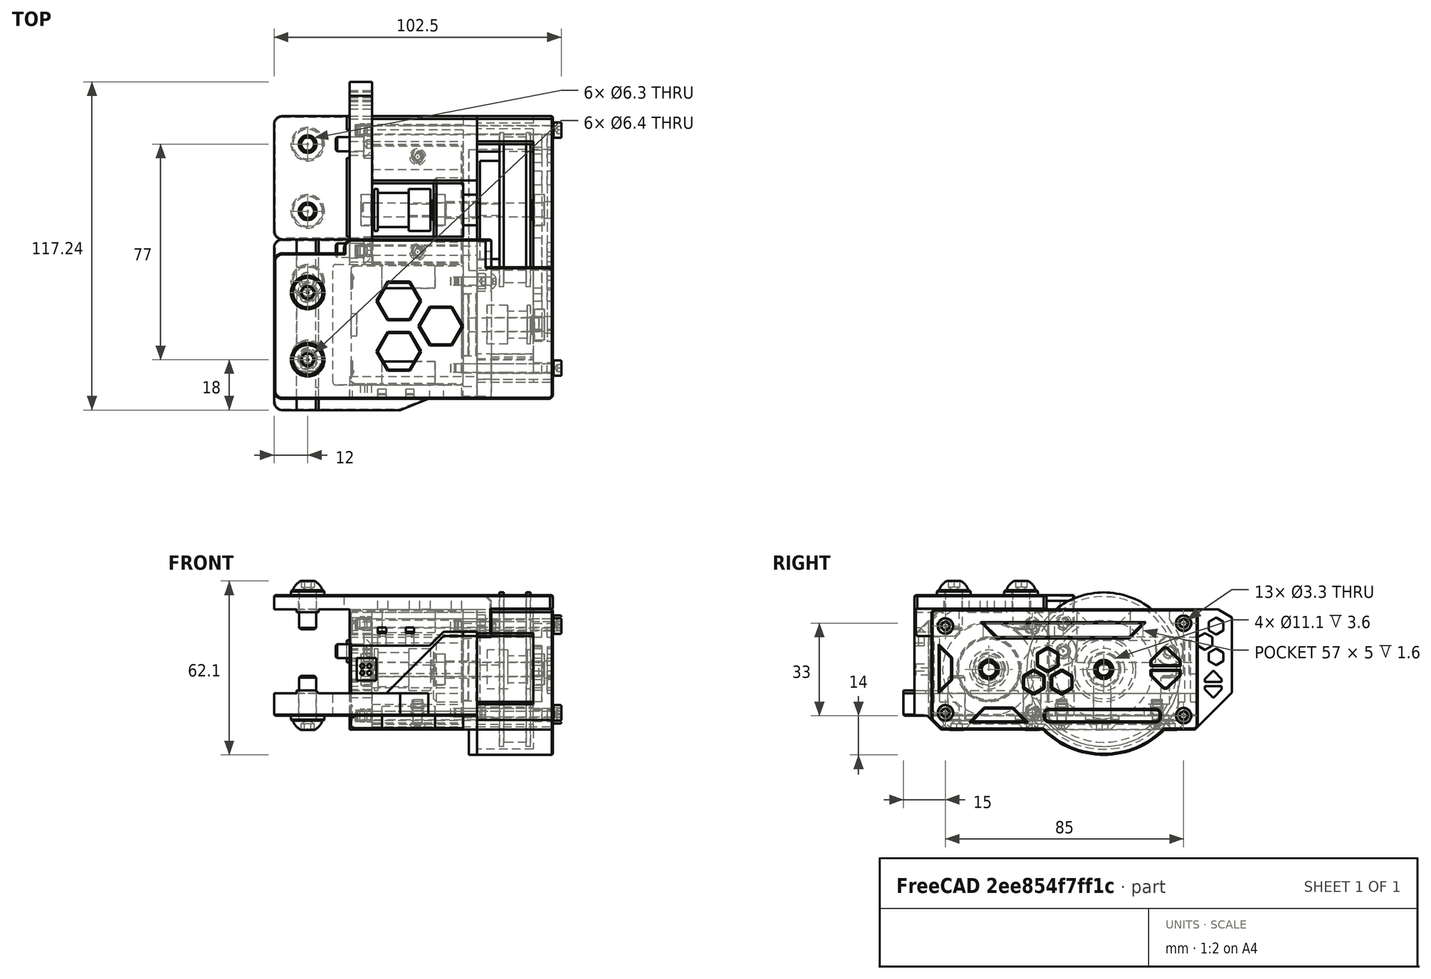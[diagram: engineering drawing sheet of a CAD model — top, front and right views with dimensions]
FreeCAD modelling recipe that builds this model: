
FCSTD DOCUMENT  (FreeCAD 0.19R24291 (Git))
Label: z-motor-right-assembly
License: Other
LicenseURL: GPL3
objects: Part::FeaturePython×27, Part::Feature×18, PartDesign::CoordinateSystem×1, App::Part×1
note: 46 computed .brp shape members not serialized (recipe doc carries the construction recipe); baked Part::Feature solids carry a one-line shape summary decoded from their .brp

FEATURE [Part::Feature] Cut001024010001  label="motor-spacer"
  shape: bbox 0.5 x 6.9 x 6.9 mm, 4 faces (baked)
FEATURE [Part::Feature] Cut001004001  label="MR115ZZ006"
  shape: bbox 4 x 11 x 11 mm, 4 faces (baked)
FEATURE [Part::Feature] Cut001024010002  label="20t-9mm-pulley001"
  shape: bbox 20 x 15 x 15 mm, 8 faces (baked)
FEATURE [Part::Feature] Cut001005001  label="MR115ZZ005"
  shape: bbox 4 x 11 x 11 mm, 4 faces (baked)
FEATURE [Part::Feature] Cut001024007001  label="motor-spacer001"
  shape: bbox 0.5 x 6.9 x 6.9 mm, 4 faces (baked)
FEATURE [Part::Feature] Cut001003001  label="MR115ZZ007"
  shape: bbox 4 x 11 x 11 mm, 4 faces (baked)
FEATURE [Part::Feature] Fusion006002011004053036004001001001  label="motor-40mm"
  shape: bbox 67 x 47 x 42 mm, 100 faces (baked)
FEATURE [Part::Feature] Cut001024009001  label="motor-spacer003"
  shape: bbox 0.5 x 6.9 x 6.9 mm, 4 faces (baked)
FEATURE [Part::Feature] Cut001024008001  label="motor-spacer004"
  shape: bbox 0.5 x 6.9 x 6.9 mm, 4 faces (baked)
FEATURE [Part::Feature] Cut001001001  label="16t-pulley001"
  shape: bbox 15.5 x 13.9 x 13.9 mm, 8 faces (baked)
FEATURE [Part::FeaturePython] Washer  label="M6-Washer"  # Fasteners workbench fastener (typed FeaturePython)
  Placement = pos=(-15,-12.5,35) rot=(0,0,1;0rad)
  diameter = 2
  invert = false
  matchOuter = true
  offset = 0
  type = 4
FEATURE [Part::FeaturePython] Washer001  label="M6-Washer011"  # Fasteners workbench fastener (typed FeaturePython)
  Placement = pos=(-15,11.5,35) rot=(0,0,1;0rad)
  diameter = 2
  invert = false
  matchOuter = true
  offset = 0
  type = 4
FEATURE [Part::FeaturePython] Washer002  label="M6-Washer009"  # Fasteners workbench fastener (typed FeaturePython)
  Placement = pos=(-15,-11.5,-8) rot=(1,0,0;3.14159rad)
  diameter = 2
  invert = true
  matchOuter = true
  offset = 0
  type = 4
FEATURE [Part::FeaturePython] Washer003  label="M6-Washer010"  # Fasteners workbench fastener (typed FeaturePython)
  Placement = pos=(-15,15.5,-8) rot=(1,0,0;3.14159rad)
  diameter = 2
  invert = true
  matchOuter = true
  offset = 0
  type = 4
FEATURE [Part::FeaturePython] Washer004  label="M6-Washer013"  # Fasteners workbench fastener (typed FeaturePython)
  Placement = pos=(-15,40.5,-8) rot=(1,0,0;3.14159rad)
  diameter = 2
  invert = true
  matchOuter = true
  offset = 0
  type = 4
FEATURE [Part::FeaturePython] Washer005  label="M6-Washer012"  # Fasteners workbench fastener (typed FeaturePython)
  Placement = pos=(-15,64.5,-8) rot=(1,0,0;3.14159rad)
  diameter = 2
  invert = true
  matchOuter = true
  offset = 0
  type = 4
FEATURE [Part::FeaturePython] Screw  label="M3x70-Screw"  # Fasteners workbench fastener (typed FeaturePython)
  Placement = pos=(72.5,69.5,-8) rot=(0,1,0;1.5708rad)
  diameter = 4
  invert = false
  length = 10
  lengthCustom = 70
  matchOuter = true
  offset = 0
  thread = false
  type = 33
FEATURE [Part::FeaturePython] Screw001  label="M3x35-Screw"  # Fasteners workbench fastener (typed FeaturePython)
  Placement = pos=(72.5,-15.5,-7) rot=(0,1,0;1.5708rad)
  diameter = 4
  invert = false
  length = 10
  lengthCustom = 35
  matchOuter = true
  offset = 0
  thread = false
  type = 33
FEATURE [Part::FeaturePython] Screw002  label="M3x35-Screw001"  # Fasteners workbench fastener (typed FeaturePython)
  Placement = pos=(72.5,-15.5,24) rot=(0,1,0;1.5708rad)
  diameter = 4
  invert = false
  length = 10
  lengthCustom = 35
  matchOuter = true
  offset = 0
  thread = false
  type = 33
FEATURE [Part::FeaturePython] Screw003  label="M3x70-Screw001"  # Fasteners workbench fastener (typed FeaturePython)
  Placement = pos=(72.5,69.5,25) rot=(0,1,0;1.5708rad)
  diameter = 4
  invert = false
  length = 10
  lengthCustom = 70
  matchOuter = true
  offset = 0
  thread = false
  type = 33
FEATURE [Part::FeaturePython] Screw005  label="M5x10-Screw001"  # Fasteners workbench fastener (typed FeaturePython)
  Placement = pos=(5,64.5,15) rot=(0,1,0;1.5708rad)
  diameter = 3
  invert = false
  length = 1
  lengthCustom = 10
  matchOuter = true
  offset = 0
  thread = false
  type = 39
FEATURE [Part::FeaturePython] Screw006  label="M3x8-Screw"  # Fasteners workbench fastener (typed FeaturePython)
  Placement = pos=(45.5,15.5,-7) rot=(0,1,0;1.5708rad)
  diameter = 4
  invert = false
  length = 10
  lengthCustom = 8
  matchOuter = true
  offset = 0
  thread = false
  type = 33
FEATURE [Part::FeaturePython] Screw007  label="M3x12-Screw"  # Fasteners workbench fastener (typed FeaturePython)
  Placement = pos=(50.5,15.5,24) rot=(0,1,0;1.5708rad)
  diameter = 1
  invert = false
  length = 3
  lengthCustom = 12
  matchOuter = true
  offset = 0
  thread = false
  type = 39
FEATURE [Part::FeaturePython] Screw008  label="M6x14-Screw"  # Fasteners workbench fastener (typed FeaturePython)
  Placement = pos=(-15,11.5,36.8) rot=(0,0,1;0rad)
  baseObject = -> Washer001 [Edge1]
  diameter = 4
  invert = false
  length = 2
  lengthCustom = 14
  matchOuter = true
  offset = 0
  thread = false
  type = 39
FEATURE [Part::FeaturePython] Screw009  label="M6x14-Screw001"  # Fasteners workbench fastener (typed FeaturePython)
  Placement = pos=(-15,-12.5,36.8) rot=(0,0,1;0rad)
  baseObject = -> Washer [Edge1]
  diameter = 4
  invert = false
  length = 2
  lengthCustom = 14
  matchOuter = true
  offset = 0
  thread = false
  type = 39
FEATURE [Part::FeaturePython] Screw010  label="M6x16-Screw004"  # Fasteners workbench fastener (typed FeaturePython)
  Placement = pos=(-15,64.5,-9.8) rot=(-1,0,0;3.14159rad)
  baseObject = -> Washer005 [Edge1]
  diameter = 4
  invert = false
  length = 3
  lengthCustom = 16
  matchOuter = true
  offset = 0
  thread = false
  type = 39
FEATURE [Part::FeaturePython] Screw011  label="M6x16-Screw005"  # Fasteners workbench fastener (typed FeaturePython)
  Placement = pos=(-15,40.5,-9.8) rot=(-1,0,0;3.14159rad)
  baseObject = -> Washer004 [Edge1]
  diameter = 4
  invert = false
  length = 3
  lengthCustom = 16
  matchOuter = true
  offset = 0
  thread = false
  type = 39
FEATURE [Part::FeaturePython] Screw012  label="M6x16-Screw001"  # Fasteners workbench fastener (typed FeaturePython)
  Placement = pos=(-15,15.5,-9.8) rot=(1,0,0;3.14159rad)
  baseObject = -> Washer003 [Edge1]
  diameter = 4
  invert = false
  length = 3
  lengthCustom = 16
  matchOuter = true
  offset = 0
  thread = false
  type = 39
FEATURE [Part::FeaturePython] Screw013  label="M6x16-Screw"  # Fasteners workbench fastener (typed FeaturePython)
  Placement = pos=(-15,-11.5,-9.8) rot=(1,0,0;3.14159rad)
  baseObject = -> Washer002 [Edge1]
  diameter = 4
  invert = false
  length = 3
  lengthCustom = 16
  matchOuter = true
  offset = 0
  thread = false
  type = 39
FEATURE [Part::Feature] Cut001024014003001002002  label="80t-pulley"
  Placement = pos=(64.5,41,8.5) rot=(0,-1,0;1.5708rad)
  shape: bbox 18 x 55 x 55 mm, 10 faces (baked)
FEATURE [Part::Feature] Body002  label="5x65-shaft"
  Placement = pos=(4.5,41,8.5) rot=(0,0,1;0rad)
  shape: bbox 65 x 5 x 5 mm, 11 faces (baked)
FEATURE [Part::Feature] Cut001024014003001002003  label="MR115ZZ008"
  Placement = pos=(-26,0,0) rot=(0,0,1;0rad)
  shape: bbox 4 x 11 x 11 mm, 4 faces (baked)
FEATURE [Part::FeaturePython] HeatSet  label="M3x4-HeatSet"  # WARN: FeaturePython — macro-defined, semantics opaque (R4)
  Placement = pos=(8,26.5,25) rot=(0,1,0;1.5708rad)
  diameter = 2
  invert = false
  offset = 0
FEATURE [Part::FeaturePython] HeatSet001  label="M3x4-HeatSet001"  # WARN: FeaturePython — macro-defined, semantics opaque (R4)
  Placement = pos=(8,69.5,25) rot=(0,1,0;1.5708rad)
  diameter = 2
  invert = false
  offset = 0
FEATURE [Part::FeaturePython] HeatSet002  label="M3x4-HeatSet002"  # WARN: FeaturePython — macro-defined, semantics opaque (R4)
  Placement = pos=(8,69.5,-8) rot=(0,1,0;1.5708rad)
  diameter = 2
  invert = false
  offset = 0
FEATURE [PartDesign::CoordinateSystem] LCS_z_motor_right  label="LCS_z-motor-right"
  AttacherType = Attacher::AttachEngine3D
FEATURE [Part::FeaturePython] HeatSet003  label="M3x3-HeatSet"  # WARN: FeaturePython — macro-defined, semantics opaque (R4)
  Placement = pos=(24.25,60,-8) rot=(1,0,0;3.14159rad)
  diameter = 2
  invert = true
  offset = 0
FEATURE [Part::FeaturePython] HeatSet004  label="M3x3-HeatSet001"  # WARN: FeaturePython — macro-defined, semantics opaque (R4)
  Placement = pos=(24.25,26,-8) rot=(1,0,0;3.14159rad)
  diameter = 2
  invert = true
  offset = 0
FEATURE [Part::FeaturePython] Screw014  label="M3x6-Screw"  # Fasteners workbench fastener (typed FeaturePython)
  Placement = pos=(24.25,60,-11) rot=(1,0,0;3.14159rad)
  diameter = 1
  invert = true
  length = 0
  lengthCustom = 6
  matchOuter = true
  offset = 0
  thread = false
  type = 40
FEATURE [Part::FeaturePython] Screw015  label="M3x6-Screw001"  # Fasteners workbench fastener (typed FeaturePython)
  Placement = pos=(24.25,26,-11) rot=(1,0,0;3.14159rad)
  diameter = 1
  invert = true
  length = 0
  lengthCustom = 6
  matchOuter = true
  offset = 0
  thread = false
  type = 40
FEATURE [Part::FeaturePython] Screw016  label="M5x10-Screw"  # Fasteners workbench fastener (typed FeaturePython)
  Placement = pos=(5,26.5,15) rot=(0,1,0;1.5708rad)
  diameter = 3
  invert = false
  length = 1
  lengthCustom = 10
  matchOuter = true
  offset = 0
  thread = false
  type = 40
FEATURE [Part::Feature] Chamfer029006005013001001  label="bottom-right-cover"
  shape: bbox 32.25 x 42.5 x 3 mm, 14 faces (baked)
FEATURE [Part::Feature] Fusion007001001001001  label="z-motor-front-plate-right"
  shape: bbox 27 x 95 x 52 mm, 216 faces (baked)
FEATURE [Part::Feature] Cut001024014003001002006005012001  label="z-motor-back-plate-right"
  shape: bbox 35 x 65.24 x 43 mm, 88 faces (baked)
FEATURE [Part::Feature] Cut001024014003001002006005013001  label="z-motor-body-right"
  shape: bbox 72.5 x 105 x 52 mm, 105 faces (baked)
FEATURE [Part::Feature] Fusion006002011004053036004001028003011016007002001010001  label="z-motor-top-plate-right"
  shape: bbox 99.5 x 57 x 18 mm, 124 faces (baked)
FEATURE [App::Part] Part  label="z-motor-right"
  Group = -> [Cut001024010001,Cut001004001,Cut001024010002,Cut001005001,Cut001024007001,Cut001003001,Fusion006002011004053036004001001001,Cut001024009001,Cut001024008001,Cut001001001,Washer001,Screw007,Screw008,Screw009,Washer,Screw013,Screw012,Screw006,Washer003,Washer002,Screw010,Washer005,Screw005,Screw011,Washer004,Screw001,Screw002,Screw003,Screw,Cut001024014003001002002,Body002,Cut001024014003001002003,+14 more]
  Origin = -> Origin
